# Revit family: QF_Woodson_Fryer_WFRT50
name_source: partatom
category: Specialty Equipment
revit_build: Autodesk Revit MEP 2014 (Build: 20140709_2115(x64)
units: mm (PartAtom-declared; Revit-internal decimal feet)

## types (1)
- W.FRT50
    Assembly Code = E1090300
    Body = QF_Stainless-Polished
    Conn Plug = 2 of 10amp plug & lead supplied 1 element @ 2400w (240V)
    Depth = 610 mm  [stored 2.00131 ft]
    Description = Countertop Fryer
    FL Amps = 20 A
    Handle = QF_Plastic-Black-Coarse
    Height = 321 mm  [stored 1.05315 ft]
    Leg = QF_Plastic-Black-Coarse
    Manufacturer = Woodson
    Model = W.FRT50
    Phase = 1
    Type Comments = Element guards and fish plate provided
    URL = http://www.stoddart.com.au
    Volts = 240 V
    Watts = 4400 W
    Weight = 16.00 kg
    Width = 550 mm

note: [stored X ft] marks values corroborated as IEEE doubles in the binary element streams (Revit-internal decimal feet)

## geometry (parser evidence)
native form markers: Sweep x13
no freeform markers — native parametric forms only
